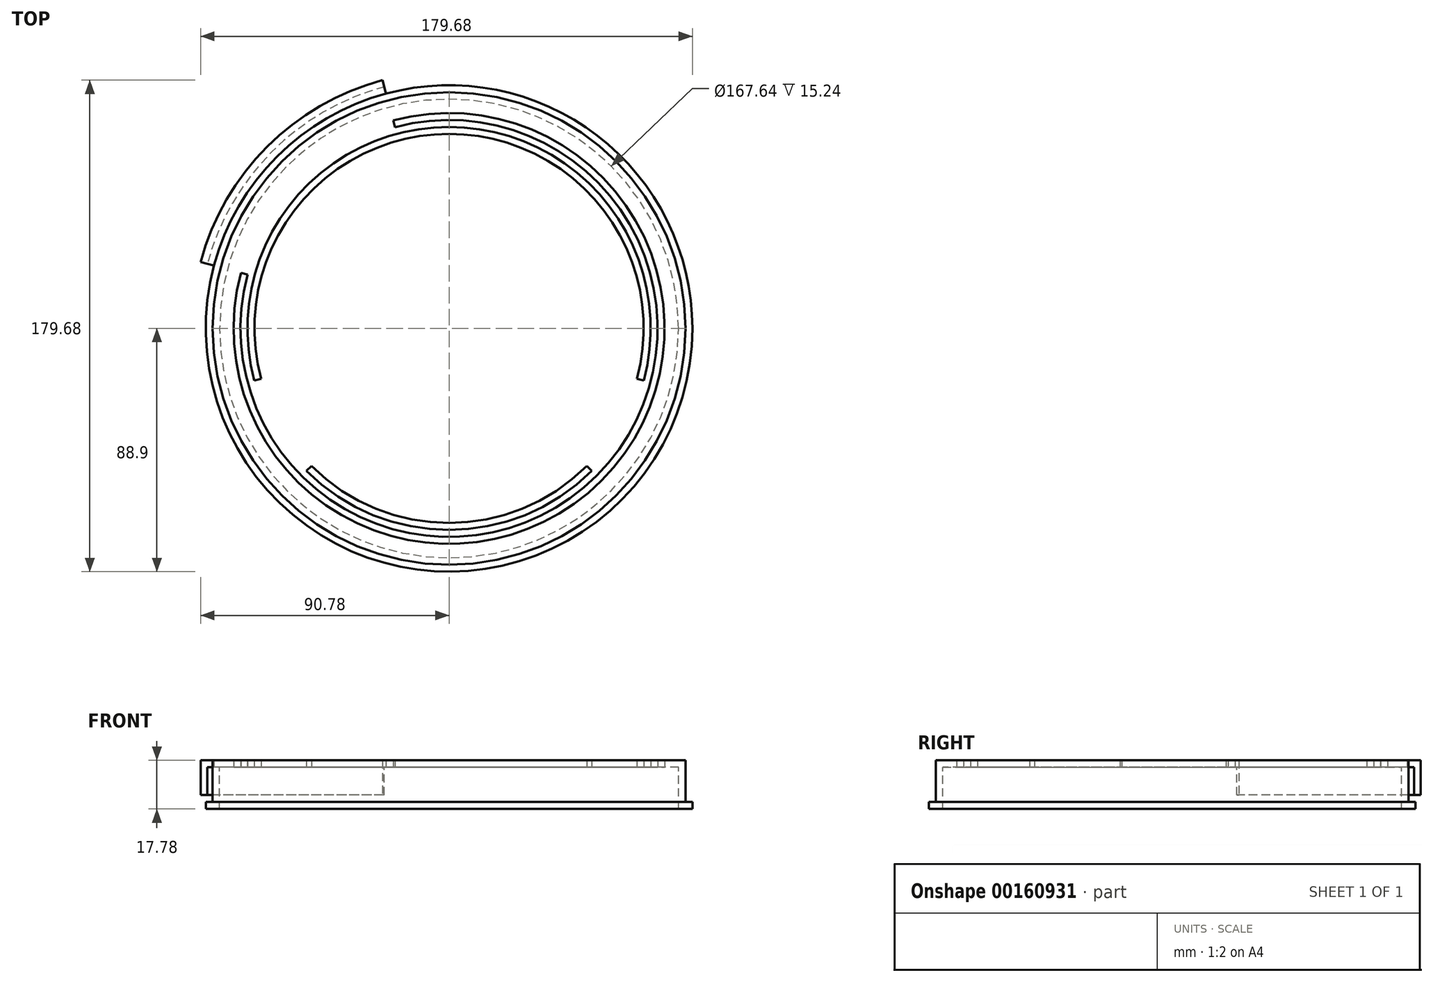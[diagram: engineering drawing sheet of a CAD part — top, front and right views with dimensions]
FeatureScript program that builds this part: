
annotation { "Feature Type Name" : "Feature", "Feature Type Description" : "" }
export const myFeature = defineFeature(function(context is Context, id is Id, definition is map)
    precondition{}
    {
        {
            var Q0;
            Q0=qCreatedBy(makeId("Top.planeOp"),FACE);
            var sketch = newSketch(context, id + "F0", { "sketchPlane" : qUnion([Q0])});
            skCircle(sketch, "E0", {"center": v(0, 0) * mm, "radius": 78.74 * mm});
            skCircle(sketch, "E1", {"center": v(0, 0) * mm, "radius": 76.2 * mm});
            skCircle(sketch, "E2", {"center": v(0, 0) * mm, "radius": 73.66 * mm});
            skCircle(sketch, "E3", {"center": v(0, 0) * mm, "radius": 71.12 * mm});
            skLineSegment(sketch, "E4", {"start": v(0, 0) * mm, "end": v(-73.6, -19.72) * mm});
            skLineSegment(sketch, "E5", {"start": v(0, 0) * mm, "end": v(-53.88, -53.88) * mm});
            skLineSegment(sketch, "E6", {"start": v(0, -94.75) * mm, "end": v(0, 89.52) * mm, "construction": true});
            skLineSegment(sketch, "E7", {"start": v(-113.22, 0) * mm, "end": v(133.16, 0) * mm, "construction": true});
            skLineSegment(sketch, "E8.MirrorCS", {"start": v(0, 0) * mm, "end": v(53.88, -53.88) * mm});
            skLineSegment(sketch, "E9.MirrorCS", {"start": v(0, 0) * mm, "end": v(73.6, -19.72) * mm});
            skLineSegment(sketch, "E10", {"start": v(-70.45, -21.5) * mm, "end": v(-72.9, -22.16) * mm});
            skLineSegment(sketch, "E11", {"start": v(53.85, -50.26) * mm, "end": v(55.65, -52.06) * mm});
            skLineSegment(sketch, "E12", {"start": v(0, 0) * mm, "end": v(19.72, 73.6) * mm});
            skLineSegment(sketch, "E13", {"start": v(0, 0) * mm, "end": v(-19.72, 73.6) * mm});
            skLineSegment(sketch, "E14", {"start": v(0, 0) * mm, "end": v(-73.6, 19.72) * mm});
            skLineSegment(sketch, "E15", {"start": v(0, 0) * mm, "end": v(-53.88, 53.88) * mm});
            skLineSegment(sketch, "E16.MirrorCS", {"start": v(0, 0) * mm, "end": v(-19.72, -73.6) * mm});
            skLineSegment(sketch, "E17.MirrorCS", {"start": v(0, 0) * mm, "end": v(19.72, -73.6) * mm});
            skLineSegment(sketch, "E18.MirrorCS", {"start": v(0, 0) * mm, "end": v(53.88, 53.88) * mm});
            skLineSegment(sketch, "E19.MirrorCS", {"start": v(0, 0) * mm, "end": v(73.6, 19.72) * mm});
            skCircle(sketch, "E20", {"center": v(0, 0) * mm, "radius": 68.58 * mm});
            skCircle(sketch, "E21", {"center": v(0, 0) * mm, "radius": 66.04 * mm});
            skCircle(sketch, "E22", {"center": v(0, 0) * mm, "radius": 63.5 * mm});
            skCircle(sketch, "E23", {"center": v(0, 0) * mm, "radius": 60.96 * mm});
            skCircle(sketch, "E24", {"center": v(0, 0) * mm, "radius": 58.42 * mm});
            skCircle(sketch, "E25", {"center": v(0, 0) * mm, "radius": 55.88 * mm});
            skCircle(sketch, "E26", {"center": v(0, 0) * mm, "radius": 50.8 * mm});
            skCircle(sketch, "E27", {"center": v(0, 0) * mm, "radius": 53.34 * mm});
            skCircle(sketch, "E28", {"center": v(0, 0) * mm, "radius": 48.26 * mm});
            skCircle(sketch, "E29", {"center": v(0, 0) * mm, "radius": 45.72 * mm});
            skCircle(sketch, "E30", {"center": v(0, 0) * mm, "radius": 43.18 * mm});
            skCircle(sketch, "E31", {"center": v(0, 0) * mm, "radius": 40.64 * mm});
            skCircle(sketch, "E32", {"center": v(0, 0) * mm, "radius": 38.1 * mm});
            skCircle(sketch, "E33", {"center": v(0, 0) * mm, "radius": 35.56 * mm});
            skCircle(sketch, "E34", {"center": v(0, 0) * mm, "radius": 33.02 * mm});
            skCircle(sketch, "E35", {"center": v(0, 0) * mm, "radius": 30.48 * mm});
            skCircle(sketch, "E36", {"center": v(0, 0) * mm, "radius": 27.94 * mm});
            skCircle(sketch, "E37", {"center": v(0, 0) * mm, "radius": 25.4 * mm});
            skCircle(sketch, "E38", {"center": v(0, 0) * mm, "radius": 81.28 * mm});
            skCircle(sketch, "E39", {"center": v(0, 0) * mm, "radius": 83.82 * mm});
            skCircle(sketch, "E40", {"center": v(0, 0) * mm, "radius": 86.36 * mm});
            skCircle(sketch, "E41", {"center": v(0, 0) * mm, "radius": 88.9 * mm});
            skLineSegment(sketch, "E42", {"start": v(0, 0) * mm, "end": v(-62.86, 62.86) * mm});
            skLineSegment(sketch, "E43.MirrorCS", {"start": v(0, 0) * mm, "end": v(62.86, 62.86) * mm});
            skLineSegment(sketch, "E44.MirrorCS", {"start": v(0, 0) * mm, "end": v(62.86, -62.86) * mm});
            skLineSegment(sketch, "E45.MirrorCS", {"start": v(0, 0) * mm, "end": v(-62.86, -62.86) * mm});
            skLineSegment(sketch, "E46", {"start": v(0, 0) * mm, "end": v(-85.87, 23) * mm});
            skLineSegment(sketch, "E47", {"start": v(0, 0) * mm, "end": v(-23, 85.87) * mm});
            skCircle(sketch, "E48", {"center": v(0, 0) * mm, "radius": 91.44 * mm});
            skLineSegment(sketch, "E49", {"start": v(-73.6, 19.72) * mm, "end": v(-90.78, 24.32) * mm});
            skLineSegment(sketch, "E50", {"start": v(-53.88, 53.88) * mm, "end": v(-66.45, 66.45) * mm});
            skLineSegment(sketch, "E51", {"start": v(-19.72, 73.6) * mm, "end": v(-24.32, 90.78) * mm});
            skCircle(sketch, "E52", {"center": v(0, 0) * mm, "radius": 93.98 * mm});
            skSolve(sketch);
        }
        {
            var Q0;
            Q0=qCreatedBy(makeId("Front.planeOp"),FACE);
            var sketch = newSketch(context, id + "F1", { "sketchPlane" : qUnion([Q0])});
            skLineSegment(sketch, "E53", {"start": v(0, -55.97) * mm, "end": v(0, 75.19) * mm, "construction": true});
            skSolve(sketch);
        }
        {
            var Q0;
            {var subQ0=sQuery(id+"F0.wireOp",EDGE,"E51");var subQ1=sQuery(id+"F0.wireOp",EDGE,"E39");var subQ2=makeQuery(id+"F0.imprint","INTERSECT",VERTEX,{"derivedFrom":[subQ1,subQ0]});Q0=makeQuery(id+"F0.imprint","IMPRINT",FACE,{"disambiguationData":[TD([[makeQuery(id+"F0.imprint","IMPRINT",EDGE,{"disambiguationData":[TD([[subQ2,-1.0]])],"derivedFrom":subQ1}),-1.0]])]});}
            var Q1;
            {var subQ0=sQuery(id+"F0.wireOp",EDGE,"E42");var subQ1=sQuery(id+"F0.wireOp",EDGE,"E35");var subQ2=makeQuery(id+"F0.imprint","INTERSECT",VERTEX,{"derivedFrom":[subQ1,subQ0]});Q1=makeQuery(id+"F0.imprint","IMPRINT",FACE,{"disambiguationData":[TD([[makeQuery(id+"F0.imprint","IMPRINT",EDGE,{"disambiguationData":[TD([[subQ2,-1.0]])],"derivedFrom":subQ1}),1.0]])]});}
            var Q2;
            {var subQ0=sQuery(id+"F0.wireOp",EDGE,"E42");var subQ1=sQuery(id+"F0.wireOp",EDGE,"E31");var subQ2=makeQuery(id+"F0.imprint","INTERSECT",VERTEX,{"derivedFrom":[subQ1,subQ0]});Q2=makeQuery(id+"F0.imprint","IMPRINT",FACE,{"disambiguationData":[TD([[makeQuery(id+"F0.imprint","IMPRINT",EDGE,{"disambiguationData":[TD([[subQ2,-1.0]])],"derivedFrom":subQ1}),1.0]])]});}
            var Q3;
            {var subQ0=sQuery(id+"F0.wireOp",EDGE,"E42");var subQ1=sQuery(id+"F0.wireOp",EDGE,"E26");var subQ2=makeQuery(id+"F0.imprint","INTERSECT",VERTEX,{"derivedFrom":[subQ1,subQ0]});Q3=makeQuery(id+"F0.imprint","IMPRINT",FACE,{"disambiguationData":[TD([[makeQuery(id+"F0.imprint","IMPRINT",EDGE,{"disambiguationData":[TD([[subQ2,-1.0]])],"derivedFrom":subQ1}),1.0]])]});}
            var Q4;
            {var subQ0=sQuery(id+"F0.wireOp",EDGE,"E42");var subQ1=sQuery(id+"F0.wireOp",EDGE,"E3");var subQ2=makeQuery(id+"F0.imprint","INTERSECT",VERTEX,{"derivedFrom":[subQ1,subQ0]});Q4=makeQuery(id+"F0.imprint","IMPRINT",FACE,{"disambiguationData":[TD([[makeQuery(id+"F0.imprint","IMPRINT",EDGE,{"disambiguationData":[TD([[subQ2,-1.0]])],"derivedFrom":subQ1}),1.0]])]});}
            var Q5;
            {var subQ0=sQuery(id+"F0.wireOp",EDGE,"E50");var subQ1=sQuery(id+"F0.wireOp",EDGE,"E0");var subQ2=makeQuery(id+"F0.imprint","INTERSECT",VERTEX,{"derivedFrom":[subQ1,subQ0]});Q5=makeQuery(id+"F0.imprint","IMPRINT",FACE,{"disambiguationData":[TD([[makeQuery(id+"F0.imprint","IMPRINT",EDGE,{"disambiguationData":[TD([[subQ2,-1.0]])],"derivedFrom":subQ1}),-1.0]])]});}
            var Q6;
            {var subQ0=sQuery(id+"F0.wireOp",EDGE,"E42");var subQ1=sQuery(id+"F0.wireOp",EDGE,"E23");var subQ2=makeQuery(id+"F0.imprint","INTERSECT",VERTEX,{"derivedFrom":[subQ1,subQ0]});Q6=makeQuery(id+"F0.imprint","IMPRINT",FACE,{"disambiguationData":[TD([[makeQuery(id+"F0.imprint","IMPRINT",EDGE,{"disambiguationData":[TD([[subQ2,-1.0]])],"derivedFrom":subQ1}),1.0]])]});}
            var Q7;
            {var subQ0=sQuery(id+"F0.wireOp",EDGE,"E47");var subQ1=sQuery(id+"F0.wireOp",EDGE,"E29");var subQ2=makeQuery(id+"F0.imprint","INTERSECT",VERTEX,{"derivedFrom":[subQ1,subQ0]});Q7=makeQuery(id+"F0.imprint","IMPRINT",FACE,{"disambiguationData":[TD([[makeQuery(id+"F0.imprint","IMPRINT",EDGE,{"disambiguationData":[TD([[subQ2,-1.0]])],"derivedFrom":subQ1}),1.0]])]});}
            var Q8;
            {var subQ0=sQuery(id+"F0.wireOp",EDGE,"E47");var subQ1=sQuery(id+"F0.wireOp",EDGE,"E25");var subQ2=makeQuery(id+"F0.imprint","INTERSECT",VERTEX,{"derivedFrom":[subQ1,subQ0]});Q8=makeQuery(id+"F0.imprint","IMPRINT",FACE,{"disambiguationData":[TD([[makeQuery(id+"F0.imprint","IMPRINT",EDGE,{"disambiguationData":[TD([[subQ2,-1.0]])],"derivedFrom":subQ1}),1.0]])]});}
            var Q9;
            {var subQ0=sQuery(id+"F0.wireOp",EDGE,"E47");var subQ1=sQuery(id+"F0.wireOp",EDGE,"E21");var subQ2=makeQuery(id+"F0.imprint","INTERSECT",VERTEX,{"derivedFrom":[subQ1,subQ0]});Q9=makeQuery(id+"F0.imprint","IMPRINT",FACE,{"disambiguationData":[TD([[makeQuery(id+"F0.imprint","IMPRINT",EDGE,{"disambiguationData":[TD([[subQ2,-1.0]])],"derivedFrom":subQ1}),1.0]])]});}
            var Q10;
            {var subQ3=sQuery(id+"F0.wireOp",EDGE,"E47");var subQ5=sQuery(id+"F0.wireOp",EDGE,"E2");var subQ6=makeQuery(id+"F0.imprint","INTERSECT",VERTEX,{"derivedFrom":[subQ5,subQ3]});Q10=makeQuery(id+"F0.imprint","IMPRINT",FACE,{"disambiguationData":[TD([[makeQuery(id+"F0.imprint","IMPRINT",EDGE,{"disambiguationData":[TD([[subQ6,-1.0]])],"derivedFrom":subQ5}),-1.0]])]});}
            var Q11;
            {var subQ0=sQuery(id+"F0.wireOp",EDGE,"E50");var subQ1=sQuery(id+"F0.wireOp",EDGE,"0hvVO4CU-wei3-HGFo-vqJD-OmLTcpI8bHwh");var subQ2=makeQuery(id+"F0.imprint","INTERSECT",VERTEX,{"derivedFrom":[subQ1,subQ0]});Q11=makeQuery(id+"F0.imprint","IMPRINT",FACE,{"disambiguationData":[TD([[makeQuery(id+"F0.imprint","IMPRINT",EDGE,{"disambiguationData":[TD([[subQ2,1.0]])],"derivedFrom":subQ1}),1.0]])]});}
            var Q12;
            {var subQ0=sQuery(id+"F0.wireOp",EDGE,"E50");var subQ1=sQuery(id+"F0.wireOp",EDGE,"E41");var subQ2=makeQuery(id+"F0.imprint","INTERSECT",VERTEX,{"derivedFrom":[subQ1,subQ0]});Q12=makeQuery(id+"F0.imprint","IMPRINT",FACE,{"disambiguationData":[TD([[makeQuery(id+"F0.imprint","IMPRINT",EDGE,{"disambiguationData":[TD([[subQ2,-1.0]])],"derivedFrom":subQ1}),-1.0]])]});}
            var Q13;
            {var subQ0=sQuery(id+"F0.wireOp",EDGE,"E49");var subQ1=sQuery(id+"F0.wireOp",EDGE,"0hvVO4CU-wei3-HGFo-vqJD-OmLTcpI8bHwh");var subQ2=makeQuery(id+"F0.imprint","INTERSECT",VERTEX,{"derivedFrom":[subQ1,subQ0]});Q13=makeQuery(id+"F0.imprint","IMPRINT",FACE,{"disambiguationData":[TD([[makeQuery(id+"F0.imprint","IMPRINT",EDGE,{"disambiguationData":[TD([[subQ2,1.0]])],"derivedFrom":subQ1}),1.0]])]});}
            var Q14;
            {var subQ0=sQuery(id+"F0.wireOp",EDGE,"E51");var subQ1=sQuery(id+"F0.wireOp",EDGE,"E41");var subQ2=makeQuery(id+"F0.imprint","INTERSECT",VERTEX,{"derivedFrom":[subQ1,subQ0]});Q14=makeQuery(id+"F0.imprint","IMPRINT",FACE,{"disambiguationData":[TD([[makeQuery(id+"F0.imprint","IMPRINT",EDGE,{"disambiguationData":[TD([[subQ2,-1.0]])],"derivedFrom":subQ1}),-1.0]])]});}
            var Q15;
            {var subQ0=sQuery(id+"F0.wireOp",EDGE,"E47");var subQ1=sQuery(id+"F0.wireOp",EDGE,"E33");var subQ2=makeQuery(id+"F0.imprint","INTERSECT",VERTEX,{"derivedFrom":[subQ1,subQ0]});Q15=makeQuery(id+"F0.imprint","IMPRINT",FACE,{"disambiguationData":[TD([[makeQuery(id+"F0.imprint","IMPRINT",EDGE,{"disambiguationData":[TD([[subQ2,-1.0]])],"derivedFrom":subQ1}),1.0]])]});}
            var Q16;
            {var subQ0=sQuery(id+"F0.wireOp",EDGE,"E50");var subQ1=sQuery(id+"F0.wireOp",EDGE,"E38");var subQ2=makeQuery(id+"F0.imprint","INTERSECT",VERTEX,{"derivedFrom":[subQ1,subQ0]});Q16=makeQuery(id+"F0.imprint","IMPRINT",FACE,{"disambiguationData":[TD([[makeQuery(id+"F0.imprint","IMPRINT",EDGE,{"disambiguationData":[TD([[subQ2,-1.0]])],"derivedFrom":subQ1}),-1.0]])]});}
            var Q17;
            {var subQ0=sQuery(id+"F0.wireOp",EDGE,"E42");var subQ1=sQuery(id+"F0.wireOp",EDGE,"E2");var subQ2=makeQuery(id+"F0.imprint","INTERSECT",VERTEX,{"derivedFrom":[subQ1,subQ0]});Q17=makeQuery(id+"F0.imprint","IMPRINT",FACE,{"disambiguationData":[TD([[makeQuery(id+"F0.imprint","IMPRINT",EDGE,{"disambiguationData":[TD([[subQ2,-1.0]])],"derivedFrom":subQ1}),1.0]])]});}
            var Q18;
            {var subQ0=sQuery(id+"F0.wireOp",EDGE,"E42");var subQ1=sQuery(id+"F0.wireOp",EDGE,"E22");var subQ2=makeQuery(id+"F0.imprint","INTERSECT",VERTEX,{"derivedFrom":[subQ1,subQ0]});Q18=makeQuery(id+"F0.imprint","IMPRINT",FACE,{"disambiguationData":[TD([[makeQuery(id+"F0.imprint","IMPRINT",EDGE,{"disambiguationData":[TD([[subQ2,-1.0]])],"derivedFrom":subQ1}),1.0]])]});}
            var Q19;
            {var subQ0=sQuery(id+"F0.wireOp",EDGE,"E42");var subQ1=sQuery(id+"F0.wireOp",EDGE,"E27");var subQ2=makeQuery(id+"F0.imprint","INTERSECT",VERTEX,{"derivedFrom":[subQ1,subQ0]});Q19=makeQuery(id+"F0.imprint","IMPRINT",FACE,{"disambiguationData":[TD([[makeQuery(id+"F0.imprint","IMPRINT",EDGE,{"disambiguationData":[TD([[subQ2,-1.0]])],"derivedFrom":subQ1}),1.0]])]});}
            var Q20;
            {var subQ0=sQuery(id+"F0.wireOp",EDGE,"E42");var subQ1=sQuery(id+"F0.wireOp",EDGE,"E30");var subQ2=makeQuery(id+"F0.imprint","INTERSECT",VERTEX,{"derivedFrom":[subQ1,subQ0]});Q20=makeQuery(id+"F0.imprint","IMPRINT",FACE,{"disambiguationData":[TD([[makeQuery(id+"F0.imprint","IMPRINT",EDGE,{"disambiguationData":[TD([[subQ2,-1.0]])],"derivedFrom":subQ1}),1.0]])]});}
            var Q21;
            {var subQ0=sQuery(id+"F0.wireOp",EDGE,"E42");var subQ1=sQuery(id+"F0.wireOp",EDGE,"E34");var subQ2=makeQuery(id+"F0.imprint","INTERSECT",VERTEX,{"derivedFrom":[subQ1,subQ0]});Q21=makeQuery(id+"F0.imprint","IMPRINT",FACE,{"disambiguationData":[TD([[makeQuery(id+"F0.imprint","IMPRINT",EDGE,{"disambiguationData":[TD([[subQ2,-1.0]])],"derivedFrom":subQ1}),1.0]])]});}
            var Q22;
            {var subQ0=sQuery(id+"F0.wireOp",EDGE,"E47");var subQ1=sQuery(id+"F0.wireOp",EDGE,"E36");var subQ2=makeQuery(id+"F0.imprint","INTERSECT",VERTEX,{"derivedFrom":[subQ1,subQ0]});Q22=makeQuery(id+"F0.imprint","IMPRINT",FACE,{"disambiguationData":[TD([[makeQuery(id+"F0.imprint","IMPRINT",EDGE,{"disambiguationData":[TD([[subQ2,-1.0]])],"derivedFrom":subQ1}),1.0]])]});}
            var Q23;
            {var subQ0=sQuery(id+"F0.wireOp",EDGE,"E47");var subQ1=sQuery(id+"F0.wireOp",EDGE,"E28");var subQ2=makeQuery(id+"F0.imprint","INTERSECT",VERTEX,{"derivedFrom":[subQ1,subQ0]});Q23=makeQuery(id+"F0.imprint","IMPRINT",FACE,{"disambiguationData":[TD([[makeQuery(id+"F0.imprint","IMPRINT",EDGE,{"disambiguationData":[TD([[subQ2,-1.0]])],"derivedFrom":subQ1}),1.0]])]});}
            var Q24;
            {var subQ0=sQuery(id+"F0.wireOp",EDGE,"E47");var subQ1=sQuery(id+"F0.wireOp",EDGE,"E24");var subQ2=makeQuery(id+"F0.imprint","INTERSECT",VERTEX,{"derivedFrom":[subQ1,subQ0]});Q24=makeQuery(id+"F0.imprint","IMPRINT",FACE,{"disambiguationData":[TD([[makeQuery(id+"F0.imprint","IMPRINT",EDGE,{"disambiguationData":[TD([[subQ2,-1.0]])],"derivedFrom":subQ1}),1.0]])]});}
            var Q25;
            {var subQ0=sQuery(id+"F0.wireOp",EDGE,"E47");var subQ1=sQuery(id+"F0.wireOp",EDGE,"E20");var subQ2=makeQuery(id+"F0.imprint","INTERSECT",VERTEX,{"derivedFrom":[subQ1,subQ0]});Q25=makeQuery(id+"F0.imprint","IMPRINT",FACE,{"disambiguationData":[TD([[makeQuery(id+"F0.imprint","IMPRINT",EDGE,{"disambiguationData":[TD([[subQ2,-1.0]])],"derivedFrom":subQ1}),1.0]])]});}
            var Q26;
            {var subQ0=sQuery(id+"F0.wireOp",EDGE,"E51");var subQ1=sQuery(id+"F0.wireOp",EDGE,"E0");var subQ2=makeQuery(id+"F0.imprint","INTERSECT",VERTEX,{"derivedFrom":[subQ1,subQ0]});Q26=makeQuery(id+"F0.imprint","IMPRINT",FACE,{"disambiguationData":[TD([[makeQuery(id+"F0.imprint","IMPRINT",EDGE,{"disambiguationData":[TD([[subQ2,-1.0]])],"derivedFrom":subQ1}),1.0]])]});}
            var Q27;
            {var subQ0=sQuery(id+"F0.wireOp",EDGE,"E51");var subQ1=sQuery(id+"F0.wireOp",EDGE,"E40");var subQ2=makeQuery(id+"F0.imprint","INTERSECT",VERTEX,{"derivedFrom":[subQ1,subQ0]});Q27=makeQuery(id+"F0.imprint","IMPRINT",FACE,{"disambiguationData":[TD([[makeQuery(id+"F0.imprint","IMPRINT",EDGE,{"disambiguationData":[TD([[subQ2,-1.0]])],"derivedFrom":subQ1}),-1.0]])]});}
            var Q28;
            {var subQ0=sQuery(id+"F0.wireOp",EDGE,"E47");var subQ1=sQuery(id+"F0.wireOp",EDGE,"E37");var subQ2=makeQuery(id+"F0.imprint","INTERSECT",VERTEX,{"derivedFrom":[subQ1,subQ0]});Q28=makeQuery(id+"F0.imprint","IMPRINT",FACE,{"disambiguationData":[TD([[makeQuery(id+"F0.imprint","IMPRINT",EDGE,{"disambiguationData":[TD([[subQ2,-1.0]])],"derivedFrom":subQ1}),1.0]])]});}
            var Q29;
            {var subQ0=sQuery(id+"F0.wireOp",EDGE,"E42");var subQ1=sQuery(id+"F0.wireOp",EDGE,"E37");var subQ2=makeQuery(id+"F0.imprint","INTERSECT",VERTEX,{"derivedFrom":[subQ1,subQ0]});Q29=makeQuery(id+"F0.imprint","IMPRINT",FACE,{"disambiguationData":[TD([[makeQuery(id+"F0.imprint","IMPRINT",EDGE,{"disambiguationData":[TD([[subQ2,-1.0]])],"derivedFrom":subQ1}),1.0]])]});}
            var Q30;
            {var subQ0=sQuery(id+"F0.wireOp",EDGE,"E50");var subQ1=sQuery(id+"F0.wireOp",EDGE,"E48");var subQ2=makeQuery(id+"F0.imprint","INTERSECT",VERTEX,{"derivedFrom":[subQ1,subQ0]});Q30=makeQuery(id+"F0.imprint","IMPRINT",FACE,{"disambiguationData":[TD([[makeQuery(id+"F0.imprint","IMPRINT",EDGE,{"disambiguationData":[TD([[subQ2,-1.0]])],"derivedFrom":subQ1}),-1.0]])]});}
            var Q31;
            {var subQ0=sQuery(id+"F0.wireOp",EDGE,"E50");var subQ1=sQuery(id+"F0.wireOp",EDGE,"E39");var subQ2=makeQuery(id+"F0.imprint","INTERSECT",VERTEX,{"derivedFrom":[subQ1,subQ0]});Q31=makeQuery(id+"F0.imprint","IMPRINT",FACE,{"disambiguationData":[TD([[makeQuery(id+"F0.imprint","IMPRINT",EDGE,{"disambiguationData":[TD([[subQ2,-1.0]])],"derivedFrom":subQ1}),-1.0]])]});}
            var Q32;
            {var subQ0=sQuery(id+"F0.wireOp",EDGE,"E42");var subQ5=sQuery(id+"F0.wireOp",EDGE,"E2");var subQ6=makeQuery(id+"F0.imprint","INTERSECT",VERTEX,{"derivedFrom":[subQ5,subQ0]});Q32=makeQuery(id+"F0.imprint","IMPRINT",FACE,{"disambiguationData":[TD([[makeQuery(id+"F0.imprint","IMPRINT",EDGE,{"disambiguationData":[TD([[subQ6,-1.0]])],"derivedFrom":subQ5}),-1.0]])]});}
            var Q33;
            {var subQ0=sQuery(id+"F0.wireOp",EDGE,"E42");var subQ1=sQuery(id+"F0.wireOp",EDGE,"E21");var subQ2=makeQuery(id+"F0.imprint","INTERSECT",VERTEX,{"derivedFrom":[subQ1,subQ0]});Q33=makeQuery(id+"F0.imprint","IMPRINT",FACE,{"disambiguationData":[TD([[makeQuery(id+"F0.imprint","IMPRINT",EDGE,{"disambiguationData":[TD([[subQ2,-1.0]])],"derivedFrom":subQ1}),1.0]])]});}
            var Q34;
            {var subQ0=sQuery(id+"F0.wireOp",EDGE,"E42");var subQ1=sQuery(id+"F0.wireOp",EDGE,"E25");var subQ2=makeQuery(id+"F0.imprint","INTERSECT",VERTEX,{"derivedFrom":[subQ1,subQ0]});Q34=makeQuery(id+"F0.imprint","IMPRINT",FACE,{"disambiguationData":[TD([[makeQuery(id+"F0.imprint","IMPRINT",EDGE,{"disambiguationData":[TD([[subQ2,-1.0]])],"derivedFrom":subQ1}),1.0]])]});}
            var Q35;
            {var subQ0=sQuery(id+"F0.wireOp",EDGE,"E42");var subQ1=sQuery(id+"F0.wireOp",EDGE,"E29");var subQ2=makeQuery(id+"F0.imprint","INTERSECT",VERTEX,{"derivedFrom":[subQ1,subQ0]});Q35=makeQuery(id+"F0.imprint","IMPRINT",FACE,{"disambiguationData":[TD([[makeQuery(id+"F0.imprint","IMPRINT",EDGE,{"disambiguationData":[TD([[subQ2,-1.0]])],"derivedFrom":subQ1}),1.0]])]});}
            var Q36;
            {var subQ0=sQuery(id+"F0.wireOp",EDGE,"E42");var subQ1=sQuery(id+"F0.wireOp",EDGE,"E33");var subQ2=makeQuery(id+"F0.imprint","INTERSECT",VERTEX,{"derivedFrom":[subQ1,subQ0]});Q36=makeQuery(id+"F0.imprint","IMPRINT",FACE,{"disambiguationData":[TD([[makeQuery(id+"F0.imprint","IMPRINT",EDGE,{"disambiguationData":[TD([[subQ2,-1.0]])],"derivedFrom":subQ1}),1.0]])]});}
            var Q37;
            {var subQ0=sQuery(id+"F0.wireOp",EDGE,"E47");var subQ1=sQuery(id+"F0.wireOp",EDGE,"E35");var subQ2=makeQuery(id+"F0.imprint","INTERSECT",VERTEX,{"derivedFrom":[subQ1,subQ0]});Q37=makeQuery(id+"F0.imprint","IMPRINT",FACE,{"disambiguationData":[TD([[makeQuery(id+"F0.imprint","IMPRINT",EDGE,{"disambiguationData":[TD([[subQ2,-1.0]])],"derivedFrom":subQ1}),1.0]])]});}
            var Q38;
            {var subQ0=sQuery(id+"F0.wireOp",EDGE,"E47");var subQ1=sQuery(id+"F0.wireOp",EDGE,"E32");var subQ2=makeQuery(id+"F0.imprint","INTERSECT",VERTEX,{"derivedFrom":[subQ1,subQ0]});Q38=makeQuery(id+"F0.imprint","IMPRINT",FACE,{"disambiguationData":[TD([[makeQuery(id+"F0.imprint","IMPRINT",EDGE,{"disambiguationData":[TD([[subQ2,-1.0]])],"derivedFrom":subQ1}),1.0]])]});}
            var Q39;
            {var subQ0=sQuery(id+"F0.wireOp",EDGE,"E47");var subQ1=sQuery(id+"F0.wireOp",EDGE,"E31");var subQ2=makeQuery(id+"F0.imprint","INTERSECT",VERTEX,{"derivedFrom":[subQ1,subQ0]});Q39=makeQuery(id+"F0.imprint","IMPRINT",FACE,{"disambiguationData":[TD([[makeQuery(id+"F0.imprint","IMPRINT",EDGE,{"disambiguationData":[TD([[subQ2,-1.0]])],"derivedFrom":subQ1}),1.0]])]});}
            var Q40;
            {var subQ0=sQuery(id+"F0.wireOp",EDGE,"E47");var subQ1=sQuery(id+"F0.wireOp",EDGE,"E26");var subQ2=makeQuery(id+"F0.imprint","INTERSECT",VERTEX,{"derivedFrom":[subQ1,subQ0]});Q40=makeQuery(id+"F0.imprint","IMPRINT",FACE,{"disambiguationData":[TD([[makeQuery(id+"F0.imprint","IMPRINT",EDGE,{"disambiguationData":[TD([[subQ2,-1.0]])],"derivedFrom":subQ1}),1.0]])]});}
            var Q41;
            {var subQ0=sQuery(id+"F0.wireOp",EDGE,"E47");var subQ1=sQuery(id+"F0.wireOp",EDGE,"E23");var subQ2=makeQuery(id+"F0.imprint","INTERSECT",VERTEX,{"derivedFrom":[subQ1,subQ0]});Q41=makeQuery(id+"F0.imprint","IMPRINT",FACE,{"disambiguationData":[TD([[makeQuery(id+"F0.imprint","IMPRINT",EDGE,{"disambiguationData":[TD([[subQ2,-1.0]])],"derivedFrom":subQ1}),1.0]])]});}
            var Q42;
            {var subQ0=sQuery(id+"F0.wireOp",EDGE,"E47");var subQ1=sQuery(id+"F0.wireOp",EDGE,"E3");var subQ2=makeQuery(id+"F0.imprint","INTERSECT",VERTEX,{"derivedFrom":[subQ1,subQ0]});Q42=makeQuery(id+"F0.imprint","IMPRINT",FACE,{"disambiguationData":[TD([[makeQuery(id+"F0.imprint","IMPRINT",EDGE,{"disambiguationData":[TD([[subQ2,-1.0]])],"derivedFrom":subQ1}),1.0]])]});}
            var Q43;
            {var subQ0=sQuery(id+"F0.wireOp",EDGE,"E51");var subQ1=sQuery(id+"F0.wireOp",EDGE,"E0");var subQ2=makeQuery(id+"F0.imprint","INTERSECT",VERTEX,{"derivedFrom":[subQ1,subQ0]});Q43=makeQuery(id+"F0.imprint","IMPRINT",FACE,{"disambiguationData":[TD([[makeQuery(id+"F0.imprint","IMPRINT",EDGE,{"disambiguationData":[TD([[subQ2,-1.0]])],"derivedFrom":subQ1}),-1.0]])]});}
            var Q44;
            {var subQ0=sQuery(id+"F0.wireOp",EDGE,"E50");var subQ1=sQuery(id+"F0.wireOp",EDGE,"E48");var subQ2=makeQuery(id+"F0.imprint","INTERSECT",VERTEX,{"derivedFrom":[subQ1,subQ0]});Q44=makeQuery(id+"F0.imprint","IMPRINT",FACE,{"disambiguationData":[TD([[makeQuery(id+"F0.imprint","IMPRINT",EDGE,{"disambiguationData":[TD([[subQ2,1.0]])],"derivedFrom":subQ1}),-1.0]])]});}
            extrude(context, id + "F2", {"entities" : qUnion([Q0, Q1, Q2, Q3, Q4, Q5, Q6, Q7, Q8, Q9, Q10, Q11, Q12, Q13, Q14, Q15, Q16, Q17, Q18, Q19, Q20, Q21, Q22, Q23, Q24, Q25, Q26, Q27, Q28, Q29, Q30, Q31, Q32, Q33, Q34, Q35, Q36, Q37, Q38, Q39, Q40, Q41, Q42, Q43, Q44]), "depth" : 2.54 * mm});
        }
        {
            var Q0;
            {var subQ0=sQuery(id+"F0.wireOp",EDGE,"E50");var subQ1=sQuery(id+"F0.wireOp",EDGE,"E39");var subQ2=makeQuery(id+"F0.imprint","INTERSECT",VERTEX,{"derivedFrom":[subQ1,subQ0]});Q0=makeQuery(id+"F0.imprint","IMPRINT",FACE,{"disambiguationData":[TD([[makeQuery(id+"F0.imprint","IMPRINT",EDGE,{"disambiguationData":[TD([[subQ2,-1.0]])],"derivedFrom":subQ1}),-1.0]])]});}
            var Q1;
            {var subQ0=sQuery(id+"F0.wireOp",EDGE,"E50");var subQ1=sQuery(id+"F0.wireOp",EDGE,"E40");var subQ2=makeQuery(id+"F0.imprint","INTERSECT",VERTEX,{"derivedFrom":[subQ1,subQ0]});Q1=makeQuery(id+"F0.imprint","IMPRINT",FACE,{"disambiguationData":[TD([[makeQuery(id+"F0.imprint","IMPRINT",EDGE,{"disambiguationData":[TD([[subQ2,-1.0]])],"derivedFrom":subQ1}),-1.0]])]});}
            extrude(context, id + "F3", {"entities" : qUnion([Q0, Q1]), "operationType" : NewBodyOperationType.ADD, "oppositeDirection" : true, "depth" : 15.24 * mm, "hasSecondDirection" : true, "secondDirectionOppositeDirection" : false, "secondDirectionDepth" : 2.54 * mm});
        }
        {
            var Q0;
            {var subQ0=sQuery(id+"F0.wireOp",EDGE,"E50");var subQ1=sQuery(id+"F0.wireOp",EDGE,"E40");var subQ2=makeQuery(id+"F0.imprint","INTERSECT",VERTEX,{"derivedFrom":[subQ1,subQ0]});Q0=makeQuery(id+"F0.imprint","IMPRINT",FACE,{"disambiguationData":[TD([[makeQuery(id+"F0.imprint","IMPRINT",EDGE,{"disambiguationData":[TD([[subQ2,-1.0]])],"derivedFrom":subQ1}),-1.0]])]});}
            extrude(context, id + "F4", {"entities" : qUnion([Q0]), "operationType" : NewBodyOperationType.REMOVE, "oppositeDirection" : true, "depth" : 12.7 * mm, "hasSecondDirection" : true, "secondDirectionOppositeDirection" : false, "secondDirectionDepth" : 2.54 * mm});
        }
        {
            var Q0;
            {var subQ0=sQuery(id+"F0.wireOp",EDGE,"E50");var subQ1=sQuery(id+"F0.wireOp",EDGE,"E48");var subQ2=makeQuery(id+"F0.imprint","INTERSECT",VERTEX,{"derivedFrom":[subQ1,subQ0]});Q0=makeQuery(id+"F0.imprint","IMPRINT",FACE,{"disambiguationData":[TD([[makeQuery(id+"F0.imprint","IMPRINT",EDGE,{"disambiguationData":[TD([[subQ2,-1.0]])],"derivedFrom":subQ1}),-1.0]])]});}
            var Q1;
            {var subQ0=sQuery(id+"F0.wireOp",EDGE,"E50");var subQ1=sQuery(id+"F0.wireOp",EDGE,"E48");var subQ2=makeQuery(id+"F0.imprint","INTERSECT",VERTEX,{"derivedFrom":[subQ1,subQ0]});Q1=makeQuery(id+"F0.imprint","IMPRINT",FACE,{"disambiguationData":[TD([[makeQuery(id+"F0.imprint","IMPRINT",EDGE,{"disambiguationData":[TD([[subQ2,1.0]])],"derivedFrom":subQ1}),-1.0]])]});}
            extrude(context, id + "F5", {"entities" : qUnion([Q0, Q1]), "operationType" : NewBodyOperationType.ADD, "oppositeDirection" : true, "depth" : 10.16 * mm});
        }
    });
